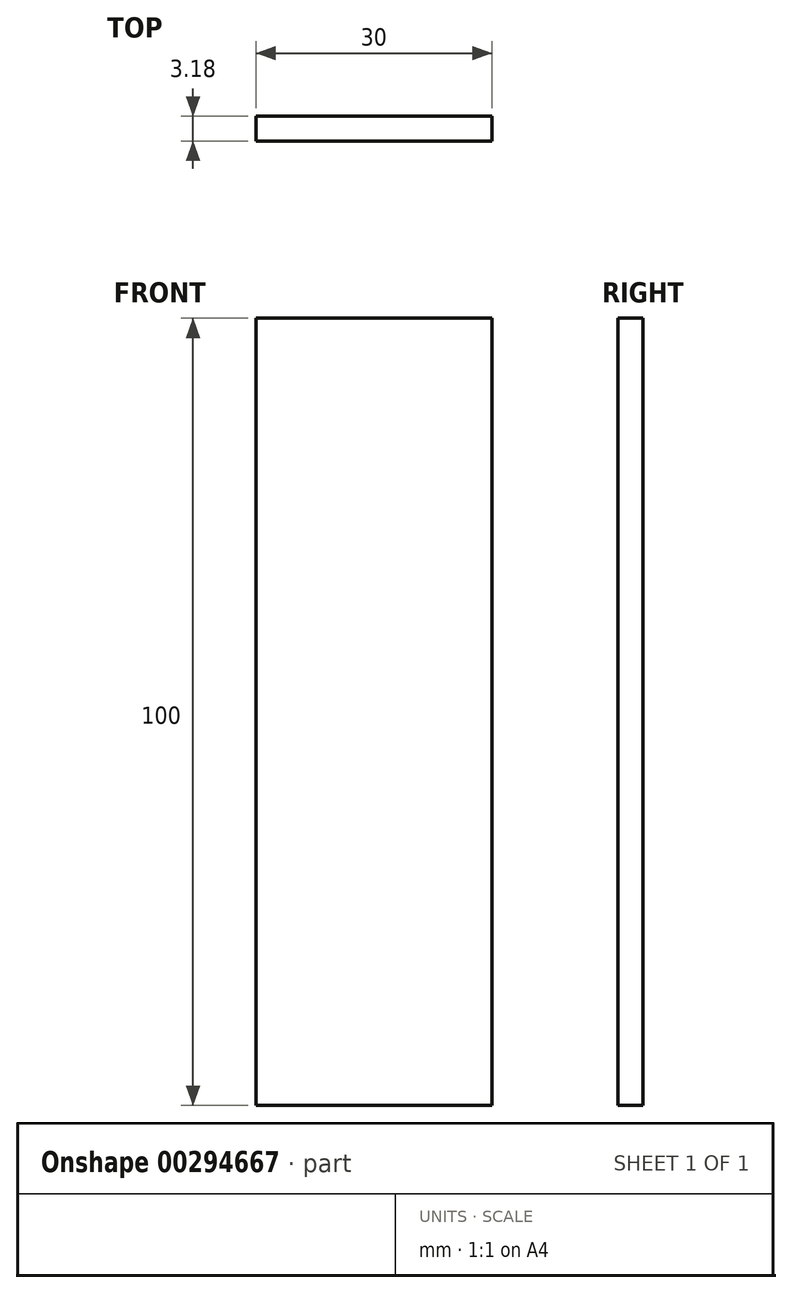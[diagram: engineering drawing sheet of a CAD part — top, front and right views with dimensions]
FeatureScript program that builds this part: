
annotation { "Feature Type Name" : "Feature", "Feature Type Description" : "" }
export const myFeature = defineFeature(function(context is Context, id is Id, definition is map)
    precondition{}
    {
        {
            var Q0;
            Q0=qCreatedBy(makeId("Front.planeOp"),FACE);
            var sketch = newSketch(context, id + "F0", { "sketchPlane" : qUnion([Q0])});
            skLineSegment(sketch, "E0.bottom", {"start": v(-15, 50) * mm, "end": v(15, 50) * mm});
            skLineSegment(sketch, "E0.top", {"start": v(-15, -50) * mm, "end": v(15, -50) * mm});
            skLineSegment(sketch, "E0.left", {"start": v(-15, 50) * mm, "end": v(-15, -50) * mm});
            skLineSegment(sketch, "E0.right", {"start": v(15, 50) * mm, "end": v(15, -50) * mm});
            skPoint(sketch, "E0.middle", {"position": v(0, 0) * mm});
            skSolve(sketch);
        }
        {
            var Q0;
            Q0 = qSketchRegion(id + "F0", true);
            extrude(context, id + "F1", {"entities" : qUnion([Q0]), "depth" : 3.18 * mm});
        }
    });
